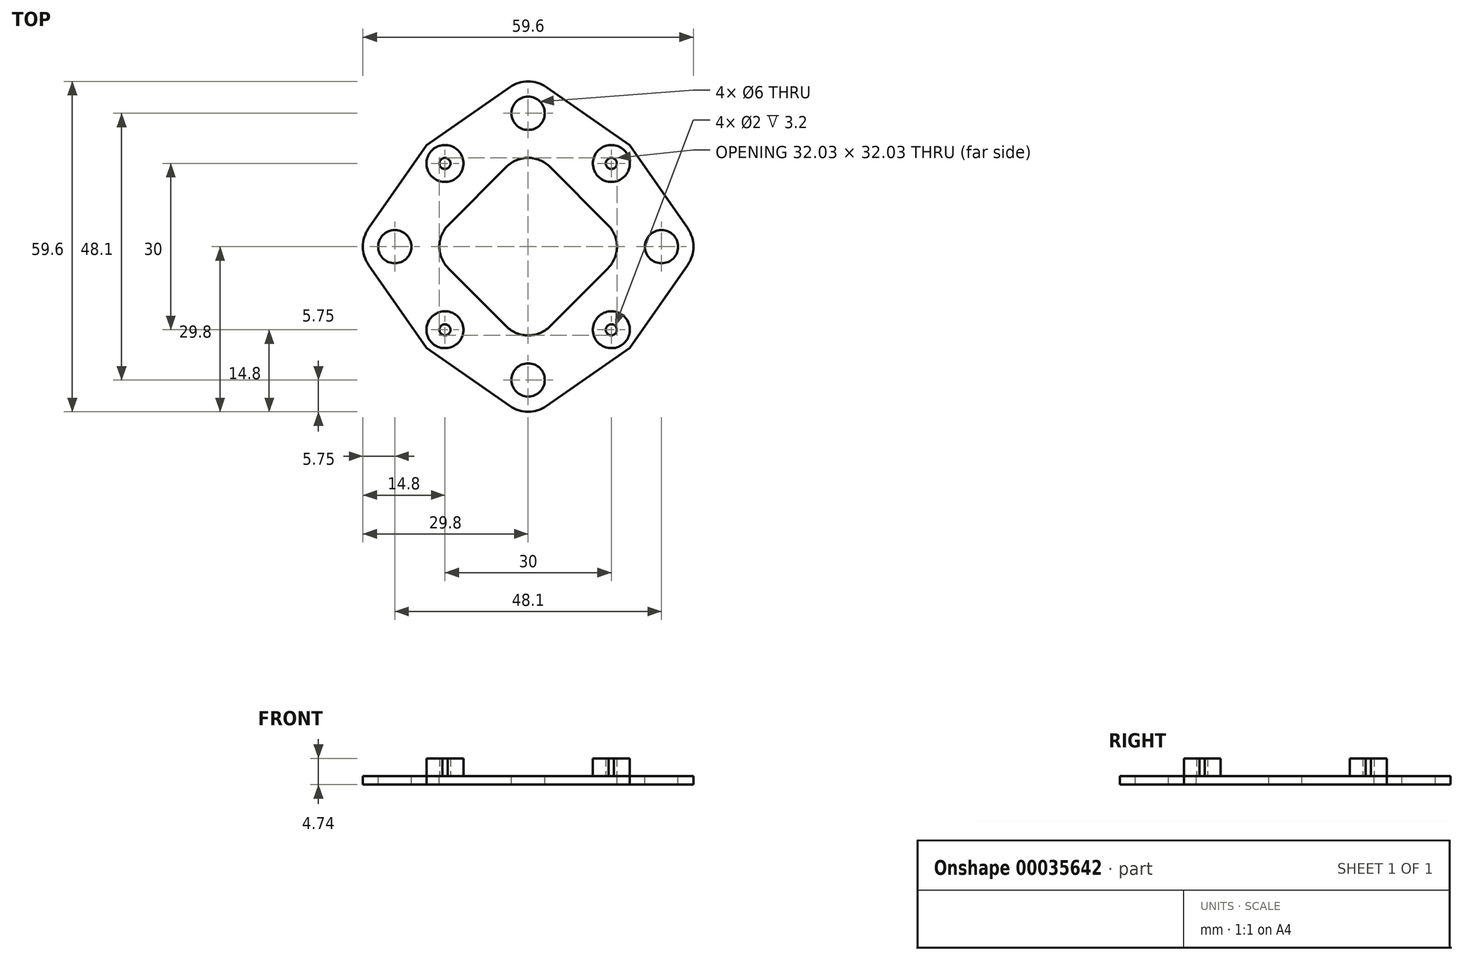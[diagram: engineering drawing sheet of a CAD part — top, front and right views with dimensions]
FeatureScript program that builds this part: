
annotation { "Feature Type Name" : "Feature", "Feature Type Description" : "" }
export const myFeature = defineFeature(function(context is Context, id is Id, definition is map)
    precondition{}
    {
        {
            var Q0;
            Q0=qCreatedBy(makeId("Top.planeOp"),FACE);
            var sketch = newSketch(context, id + "F0", { "sketchPlane" : qUnion([Q0])});
            skLineSegment(sketch, "E0", {"start": v(0, 24.05) * mm, "end": v(0, -24.05) * mm, "construction": true});
            skLineSegment(sketch, "E1", {"start": v(-36.8, 0) * mm, "end": v(35.39, 0) * mm, "construction": true});
            skLineSegment(sketch, "E2.bottom", {"start": v(-18.3, 18.3) * mm, "end": v(18.3, 18.3) * mm});
            skLineSegment(sketch, "E2.top", {"start": v(-18.3, -18.3) * mm, "end": v(18.3, -18.3) * mm});
            skLineSegment(sketch, "E2.left", {"start": v(-18.3, 18.3) * mm, "end": v(-18.3, -18.3) * mm});
            skLineSegment(sketch, "E2.right", {"start": v(18.3, 18.3) * mm, "end": v(18.3, -18.3) * mm});
            skLineSegment(sketch, "E3", {"start": v(15, 27.35) * mm, "end": v(15, 15.01) * mm, "construction": true});
            skLineSegment(sketch, "E4", {"start": v(22.4, 15) * mm, "end": v(7.6, 15) * mm, "construction": true});
            skCircle(sketch, "E5", {"center": v(15, 15) * mm, "radius": 1 * mm});
            skCircle(sketch, "E6.1.0", {"center": v(-15, 15) * mm, "radius": 1 * mm});
            skCircle(sketch, "E6.2.0", {"center": v(-15, -15) * mm, "radius": 1 * mm});
            skCircle(sketch, "E6.3.0", {"center": v(15, -15) * mm, "radius": 1 * mm});
            skPoint(sketch, "E6.center", {"position": v(0, 0) * mm});
            skCircle(sketch, "E7", {"center": v(15, 15) * mm, "radius": 3.33 * mm});
            skCircle(sketch, "E8.1.0", {"center": v(-15, 15) * mm, "radius": 3.33 * mm});
            skCircle(sketch, "E8.2.0", {"center": v(-15, -15) * mm, "radius": 3.33 * mm});
            skCircle(sketch, "E8.3.0", {"center": v(15, -15) * mm, "radius": 3.33 * mm});
            skCircle(sketch, "E9", {"center": v(0, 24.05) * mm, "radius": 5.75 * mm});
            skCircle(sketch, "E10", {"center": v(0, 24.05) * mm, "radius": 3 * mm});
            skPoint(sketch, "E11", {"position": v(-24.05, 0) * mm});
            skPoint(sketch, "E12", {"position": v(24.05, 0) * mm});
            skCircle(sketch, "E13", {"center": v(-24.05, 0) * mm, "radius": 3 * mm});
            skCircle(sketch, "E14", {"center": v(0, -24.05) * mm, "radius": 3 * mm});
            skCircle(sketch, "E15", {"center": v(24.05, 0) * mm, "radius": 3 * mm});
            skCircle(sketch, "E16", {"center": v(-24.05, 0) * mm, "radius": 5.75 * mm});
            skCircle(sketch, "E17", {"center": v(24.05, 0) * mm, "radius": 5.75 * mm});
            skCircle(sketch, "E18", {"center": v(0, -24.05) * mm, "radius": 5.75 * mm});
            skPoint(sketch, "E19", {"position": v(-18.3, 18.3) * mm});
            skPoint(sketch, "E20", {"position": v(18.3, 18.3) * mm});
            skPoint(sketch, "E21", {"position": v(18.3, -18.3) * mm});
            skLineSegment(sketch, "E22", {"start": v(-28.77, -3.29) * mm, "end": v(-18.3, -18.3) * mm});
            skLineSegment(sketch, "E23", {"start": v(-18.3, -18.3) * mm, "end": v(-3.29, -28.77) * mm});
            skLineSegment(sketch, "E24", {"start": v(-28.77, 3.29) * mm, "end": v(-18.3, 18.3) * mm});
            skLineSegment(sketch, "E25", {"start": v(-3.29, 28.77) * mm, "end": v(-18.3, 18.3) * mm});
            skLineSegment(sketch, "E26", {"start": v(18.3, 18.3) * mm, "end": v(3.29, 28.77) * mm});
            skLineSegment(sketch, "E27", {"start": v(18.3, 18.3) * mm, "end": v(28.77, 3.29) * mm});
            skLineSegment(sketch, "E28", {"start": v(18.3, -18.3) * mm, "end": v(3.29, -28.77) * mm});
            skLineSegment(sketch, "E29", {"start": v(18.3, -18.3) * mm, "end": v(28.77, -3.29) * mm});
            skLineSegment(sketch, "E30", {"start": v(-14.4, 3.9) * mm, "end": v(-3.9, 14.4) * mm});
            skLineSegment(sketch, "E31", {"start": v(3.9, 14.4) * mm, "end": v(14.4, 3.9) * mm});
            skLineSegment(sketch, "E32", {"start": v(14.4, -3.9) * mm, "end": v(3.9, -14.4) * mm});
            skLineSegment(sketch, "E33", {"start": v(-3.9, -14.4) * mm, "end": v(-14.4, -3.9) * mm});
            skPoint(sketch, "E34.visualSharp", {"position": v(0, 18.3) * mm});
            skArc(sketch, "E34.filletArc", {"start": v(3.9, 14.4) * mm, "mid": v(0, 16.02) * mm, "end": v(-3.9, 14.4) * mm});
            skPoint(sketch, "E35.visualSharp", {"position": v(18.3, 0) * mm});
            skArc(sketch, "E35.filletArc", {"start": v(14.4, -3.9) * mm, "mid": v(16.02, 0) * mm, "end": v(14.4, 3.9) * mm});
            skPoint(sketch, "E36.visualSharp", {"position": v(0, -18.3) * mm});
            skArc(sketch, "E36.filletArc", {"start": v(-3.9, -14.4) * mm, "mid": v(0, -16.02) * mm, "end": v(3.9, -14.4) * mm});
            skPoint(sketch, "E37.visualSharp", {"position": v(-18.3, 0) * mm});
            skArc(sketch, "E37.filletArc", {"start": v(-14.4, 3.9) * mm, "mid": v(-16.02, 0) * mm, "end": v(-14.4, -3.9) * mm});
            skSolve(sketch);
        }
        {
            var Q0;
            Q0=makeQuery(id+"F0.imprint","IMPRINT",FACE,{"disambiguationData":[TD([[makeQuery(id+"F0.imprint","IMPRINT",EDGE,{"derivedFrom":sQuery(id+"F0.wireOp",EDGE,"E30")}),1.0]])]});
            var Q1;
            {var subQ0=sQuery(id+"F0.wireOp",EDGE,"E25");Q1=makeQuery(id+"F0.imprint","IMPRINT",FACE,{"disambiguationData":[TD([[makeQuery(id+"F0.imprint","IMPRINT",EDGE,{"derivedFrom":subQ0}),1.0]])]});}
            var Q2;
            {var subQ0=sQuery(id+"F0.wireOp",EDGE,"E26");Q2=makeQuery(id+"F0.imprint","IMPRINT",FACE,{"disambiguationData":[TD([[makeQuery(id+"F0.imprint","IMPRINT",EDGE,{"derivedFrom":subQ0}),1.0]])]});}
            var Q3;
            Q3=makeQuery(id+"F0.imprint","IMPRINT",FACE,{"disambiguationData":[TD([[makeQuery(id+"F0.imprint","IMPRINT",EDGE,{"derivedFrom":sQuery(id+"F0.wireOp",EDGE,"E10")}),-1.0]])]});
            var Q4;
            {var subQ6=sQuery(id+"F0.wireOp",EDGE,"E27");Q4=makeQuery(id+"F0.imprint","IMPRINT",FACE,{"disambiguationData":[TD([[makeQuery(id+"F0.imprint","IMPRINT",EDGE,{"derivedFrom":subQ6}),-1.0]])]});}
            var Q5;
            {var subQ4=sQuery(id+"F0.wireOp",EDGE,"E29");Q5=makeQuery(id+"F0.imprint","IMPRINT",FACE,{"disambiguationData":[TD([[makeQuery(id+"F0.imprint","IMPRINT",EDGE,{"derivedFrom":subQ4}),1.0]])]});}
            var Q6;
            Q6=makeQuery(id+"F0.imprint","IMPRINT",FACE,{"disambiguationData":[TD([[makeQuery(id+"F0.imprint","IMPRINT",EDGE,{"derivedFrom":sQuery(id+"F0.wireOp",EDGE,"E15")}),-1.0]])]});
            var Q7;
            Q7=makeQuery(id+"F0.imprint","IMPRINT",FACE,{"disambiguationData":[TD([[makeQuery(id+"F0.imprint","IMPRINT",EDGE,{"derivedFrom":sQuery(id+"F0.wireOp",EDGE,"E6.3.0")}),-1.0]])]});
            var Q8;
            Q8=makeQuery(id+"F0.imprint","IMPRINT",FACE,{"disambiguationData":[TD([[makeQuery(id+"F0.imprint","IMPRINT",EDGE,{"derivedFrom":sQuery(id+"F0.wireOp",EDGE,"E5")}),-1.0]])]});
            var Q9;
            Q9=makeQuery(id+"F0.imprint","IMPRINT",FACE,{"disambiguationData":[TD([[makeQuery(id+"F0.imprint","IMPRINT",EDGE,{"derivedFrom":sQuery(id+"F0.wireOp",EDGE,"E5")}),1.0]])]});
            var Q10;
            {var subQ1=sQuery(id+"F0.wireOp",EDGE,"E2.bottom");var subQ3=sQuery(id+"F0.wireOp",EDGE,"E7");var subQ4=makeQuery(id+"F0.imprint","INTERSECT",VERTEX,{"disambiguationData":[OD(1.0)],"derivedFrom":[subQ1,subQ3]});Q10=makeQuery(id+"F0.imprint","IMPRINT",FACE,{"disambiguationData":[TD([[makeQuery(id+"F0.imprint","IMPRINT",EDGE,{"disambiguationData":[TD([[subQ4,1.0]])],"derivedFrom":subQ3}),-1.0]])]});}
            var Q11;
            {var subQ1=sQuery(id+"F0.wireOp",EDGE,"E2.bottom");var subQ3=sQuery(id+"F0.wireOp",EDGE,"E8.1.0");var subQ4=makeQuery(id+"F0.imprint","INTERSECT",VERTEX,{"disambiguationData":[OD(0.0)],"derivedFrom":[subQ1,subQ3]});Q11=makeQuery(id+"F0.imprint","IMPRINT",FACE,{"disambiguationData":[TD([[makeQuery(id+"F0.imprint","IMPRINT",EDGE,{"disambiguationData":[TD([[subQ4,-1.0]])],"derivedFrom":subQ3}),-1.0]])]});}
            var Q12;
            Q12=makeQuery(id+"F0.imprint","IMPRINT",FACE,{"disambiguationData":[TD([[makeQuery(id+"F0.imprint","IMPRINT",EDGE,{"derivedFrom":sQuery(id+"F0.wireOp",EDGE,"E6.1.0")}),-1.0]])]});
            var Q13;
            Q13=makeQuery(id+"F0.imprint","IMPRINT",FACE,{"disambiguationData":[TD([[makeQuery(id+"F0.imprint","IMPRINT",EDGE,{"derivedFrom":sQuery(id+"F0.wireOp",EDGE,"E6.1.0")}),1.0]])]});
            var Q14;
            Q14=makeQuery(id+"F0.imprint","IMPRINT",FACE,{"disambiguationData":[TD([[makeQuery(id+"F0.imprint","IMPRINT",EDGE,{"derivedFrom":sQuery(id+"F0.wireOp",EDGE,"E13")}),-1.0]])]});
            var Q15;
            {var subQ0=sQuery(id+"F0.wireOp",EDGE,"E24");Q15=makeQuery(id+"F0.imprint","IMPRINT",FACE,{"disambiguationData":[TD([[makeQuery(id+"F0.imprint","IMPRINT",EDGE,{"derivedFrom":subQ0}),-1.0]])]});}
            var Q16;
            {var subQ0=sQuery(id+"F0.wireOp",EDGE,"E22");Q16=makeQuery(id+"F0.imprint","IMPRINT",FACE,{"disambiguationData":[TD([[makeQuery(id+"F0.imprint","IMPRINT",EDGE,{"derivedFrom":subQ0}),1.0]])]});}
            var Q17;
            Q17=makeQuery(id+"F0.imprint","IMPRINT",FACE,{"disambiguationData":[TD([[makeQuery(id+"F0.imprint","IMPRINT",EDGE,{"derivedFrom":sQuery(id+"F0.wireOp",EDGE,"E6.2.0")}),-1.0]])]});
            var Q18;
            Q18=makeQuery(id+"F0.imprint","IMPRINT",FACE,{"disambiguationData":[TD([[makeQuery(id+"F0.imprint","IMPRINT",EDGE,{"derivedFrom":sQuery(id+"F0.wireOp",EDGE,"E6.2.0")}),1.0]])]});
            var Q19;
            {var subQ1=sQuery(id+"F0.wireOp",EDGE,"E2.top");var subQ3=sQuery(id+"F0.wireOp",EDGE,"E8.2.0");var subQ4=makeQuery(id+"F0.imprint","INTERSECT",VERTEX,{"disambiguationData":[OD(0.0)],"derivedFrom":[subQ1,subQ3]});Q19=makeQuery(id+"F0.imprint","IMPRINT",FACE,{"disambiguationData":[TD([[makeQuery(id+"F0.imprint","IMPRINT",EDGE,{"disambiguationData":[TD([[subQ4,1.0]])],"derivedFrom":subQ3}),-1.0]])]});}
            var Q20;
            {var subQ0=sQuery(id+"F0.wireOp",EDGE,"E23");Q20=makeQuery(id+"F0.imprint","IMPRINT",FACE,{"disambiguationData":[TD([[makeQuery(id+"F0.imprint","IMPRINT",EDGE,{"derivedFrom":subQ0}),1.0]])]});}
            var Q21;
            Q21=makeQuery(id+"F0.imprint","IMPRINT",FACE,{"disambiguationData":[TD([[makeQuery(id+"F0.imprint","IMPRINT",EDGE,{"derivedFrom":sQuery(id+"F0.wireOp",EDGE,"E14")}),-1.0]])]});
            var Q22;
            {var subQ0=sQuery(id+"F0.wireOp",EDGE,"E28");Q22=makeQuery(id+"F0.imprint","IMPRINT",FACE,{"disambiguationData":[TD([[makeQuery(id+"F0.imprint","IMPRINT",EDGE,{"derivedFrom":subQ0}),-1.0]])]});}
            var Q23;
            {var subQ1=sQuery(id+"F0.wireOp",EDGE,"E2.top");var subQ3=sQuery(id+"F0.wireOp",EDGE,"E8.3.0");var subQ4=makeQuery(id+"F0.imprint","INTERSECT",VERTEX,{"disambiguationData":[OD(1.0)],"derivedFrom":[subQ1,subQ3]});Q23=makeQuery(id+"F0.imprint","IMPRINT",FACE,{"disambiguationData":[TD([[makeQuery(id+"F0.imprint","IMPRINT",EDGE,{"disambiguationData":[TD([[subQ4,-1.0]])],"derivedFrom":subQ3}),-1.0]])]});}
            var Q24;
            Q24=makeQuery(id+"F0.imprint","IMPRINT",FACE,{"disambiguationData":[TD([[makeQuery(id+"F0.imprint","IMPRINT",EDGE,{"derivedFrom":sQuery(id+"F0.wireOp",EDGE,"E6.3.0")}),1.0]])]});
            var Q25;
            {var subQ0=sQuery(id+"F0.wireOp",EDGE,"E8.2.0");var subQ1=sQuery(id+"F0.wireOp",EDGE,"E2.top");var subQ2=makeQuery(id+"F0.imprint","INTERSECT",VERTEX,{"disambiguationData":[OD(0.0)],"derivedFrom":[subQ1,subQ0]});Q25=makeQuery(id+"F0.imprint","IMPRINT",FACE,{"disambiguationData":[TD([[makeQuery(id+"F0.imprint","IMPRINT",EDGE,{"disambiguationData":[TD([[subQ2,-1.0]])],"derivedFrom":subQ1}),-1.0]])]});}
            var Q26;
            {var subQ0=sQuery(id+"F0.wireOp",EDGE,"E8.2.0");var subQ1=sQuery(id+"F0.wireOp",EDGE,"E2.left");var subQ2=makeQuery(id+"F0.imprint","INTERSECT",VERTEX,{"disambiguationData":[OD(0.0)],"derivedFrom":[subQ1,subQ0]});Q26=makeQuery(id+"F0.imprint","IMPRINT",FACE,{"disambiguationData":[TD([[makeQuery(id+"F0.imprint","IMPRINT",EDGE,{"disambiguationData":[TD([[subQ2,-1.0]])],"derivedFrom":subQ1}),-1.0]])]});}
            var Q27;
            {var subQ0=sQuery(id+"F0.wireOp",EDGE,"E8.1.0");var subQ1=sQuery(id+"F0.wireOp",EDGE,"E2.left");var subQ2=makeQuery(id+"F0.imprint","INTERSECT",VERTEX,{"disambiguationData":[OD(0.0)],"derivedFrom":[subQ1,subQ0]});Q27=makeQuery(id+"F0.imprint","IMPRINT",FACE,{"disambiguationData":[TD([[makeQuery(id+"F0.imprint","IMPRINT",EDGE,{"disambiguationData":[TD([[subQ2,-1.0]])],"derivedFrom":subQ1}),-1.0]])]});}
            var Q28;
            {var subQ0=sQuery(id+"F0.wireOp",EDGE,"E8.1.0");var subQ1=sQuery(id+"F0.wireOp",EDGE,"E2.bottom");var subQ2=makeQuery(id+"F0.imprint","INTERSECT",VERTEX,{"disambiguationData":[OD(0.0)],"derivedFrom":[subQ1,subQ0]});Q28=makeQuery(id+"F0.imprint","IMPRINT",FACE,{"disambiguationData":[TD([[makeQuery(id+"F0.imprint","IMPRINT",EDGE,{"disambiguationData":[TD([[subQ2,-1.0]])],"derivedFrom":subQ1}),1.0]])]});}
            var Q29;
            {var subQ0=sQuery(id+"F0.wireOp",EDGE,"E7");var subQ1=sQuery(id+"F0.wireOp",EDGE,"E2.bottom");var subQ2=makeQuery(id+"F0.imprint","INTERSECT",VERTEX,{"disambiguationData":[OD(0.0)],"derivedFrom":[subQ1,subQ0]});Q29=makeQuery(id+"F0.imprint","IMPRINT",FACE,{"disambiguationData":[TD([[makeQuery(id+"F0.imprint","IMPRINT",EDGE,{"disambiguationData":[TD([[subQ2,-1.0]])],"derivedFrom":subQ1}),1.0]])]});}
            var Q30;
            {var subQ0=sQuery(id+"F0.wireOp",EDGE,"E7");var subQ1=sQuery(id+"F0.wireOp",EDGE,"E2.right");var subQ2=makeQuery(id+"F0.imprint","INTERSECT",VERTEX,{"disambiguationData":[OD(0.0)],"derivedFrom":[subQ1,subQ0]});Q30=makeQuery(id+"F0.imprint","IMPRINT",FACE,{"disambiguationData":[TD([[makeQuery(id+"F0.imprint","IMPRINT",EDGE,{"disambiguationData":[TD([[subQ2,-1.0]])],"derivedFrom":subQ1}),1.0]])]});}
            var Q31;
            {var subQ0=sQuery(id+"F0.wireOp",EDGE,"E8.3.0");var subQ1=sQuery(id+"F0.wireOp",EDGE,"E2.top");var subQ2=makeQuery(id+"F0.imprint","INTERSECT",VERTEX,{"disambiguationData":[OD(0.0)],"derivedFrom":[subQ1,subQ0]});Q31=makeQuery(id+"F0.imprint","IMPRINT",FACE,{"disambiguationData":[TD([[makeQuery(id+"F0.imprint","IMPRINT",EDGE,{"disambiguationData":[TD([[subQ2,-1.0]])],"derivedFrom":subQ1}),-1.0]])]});}
            var Q32;
            {var subQ0=sQuery(id+"F0.wireOp",EDGE,"E8.3.0");var subQ1=sQuery(id+"F0.wireOp",EDGE,"E2.right");var subQ2=makeQuery(id+"F0.imprint","INTERSECT",VERTEX,{"disambiguationData":[OD(0.0)],"derivedFrom":[subQ1,subQ0]});Q32=makeQuery(id+"F0.imprint","IMPRINT",FACE,{"disambiguationData":[TD([[makeQuery(id+"F0.imprint","IMPRINT",EDGE,{"disambiguationData":[TD([[subQ2,-1.0]])],"derivedFrom":subQ1}),1.0]])]});}
            extrude(context, id + "F1", {"entities" : qUnion([Q0, Q1, Q2, Q3, Q4, Q5, Q6, Q7, Q8, Q9, Q10, Q11, Q12, Q13, Q14, Q15, Q16, Q17, Q18, Q19, Q20, Q21, Q22, Q23, Q24, Q25, Q26, Q27, Q28, Q29, Q30, Q31, Q32]), "oppositeDirection" : true, "depth" : 1.54 * mm});
        }
        {
            var Q0;
            Q0=makeQuery(id+"F0.imprint","IMPRINT",FACE,{"disambiguationData":[TD([[makeQuery(id+"F0.imprint","IMPRINT",EDGE,{"derivedFrom":sQuery(id+"F0.wireOp",EDGE,"E6.2.0")}),-1.0]])]});
            var Q1;
            Q1=makeQuery(id+"F0.imprint","IMPRINT",FACE,{"disambiguationData":[TD([[makeQuery(id+"F0.imprint","IMPRINT",EDGE,{"derivedFrom":sQuery(id+"F0.wireOp",EDGE,"E6.1.0")}),-1.0]])]});
            var Q2;
            Q2=makeQuery(id+"F0.imprint","IMPRINT",FACE,{"disambiguationData":[TD([[makeQuery(id+"F0.imprint","IMPRINT",EDGE,{"derivedFrom":sQuery(id+"F0.wireOp",EDGE,"E6.3.0")}),-1.0]])]});
            var Q3;
            Q3=makeQuery(id+"F0.imprint","IMPRINT",FACE,{"disambiguationData":[TD([[makeQuery(id+"F0.imprint","IMPRINT",EDGE,{"derivedFrom":sQuery(id+"F0.wireOp",EDGE,"E5")}),-1.0]])]});
            extrude(context, id + "F2", {"entities" : qUnion([Q0, Q1, Q2, Q3]), "operationType" : NewBodyOperationType.ADD, "depth" : 3.2 * mm});
        }
    });
